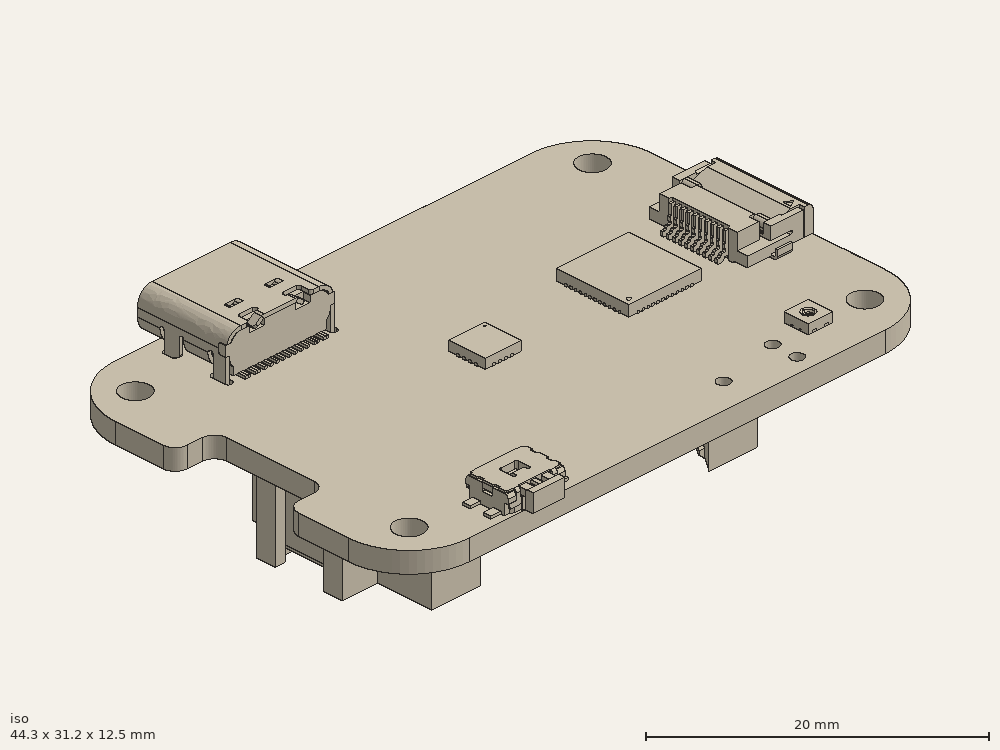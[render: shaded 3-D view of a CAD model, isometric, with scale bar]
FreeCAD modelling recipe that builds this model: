
FCSTD DOCUMENT  (FreeCAD 0.20R29410 (Git))
Label: case
License: All rights reserved
LicenseURL: http://en.wikipedia.org/wiki/All_rights_reserved
objects: Part::Feature×1, PartDesign::ShapeBinder×1, Sketcher::SketchObject×1, PartDesign::Body×1
note: 4 computed .brp shape members not serialized (recipe doc carries the construction recipe); baked Part::Feature solids carry a one-line shape summary decoded from their .brp

FEATURE [Part::Feature] Feature  label="PlantBuddy"
  Placement = pos=(-121,126,0) rot=(0,0,1;0rad)
  shape: bbox 44.33 x 31.16 x 12.48 mm, 3116 faces, 155 solids (baked)
FEATURE [PartDesign::ShapeBinder] ShapeBinder
  Placement = pos=(-143,126,0) rot=(0,0,1;0rad)
  Support = -> [Feature]
  TraceSupport = false
FEATURE [Sketcher::SketchObject] Sketch
  FullyConstrained = false
  MapMode = 5
  Support = -> [XY_Plane]
  sketch-geometry (4):
    g0: LineSegment StartX=-26.1099 StartY=15.4163 StartZ=0 EndX=26.1099 EndY=15.4163 EndZ=0
    g1: LineSegment StartX=26.1099 StartY=15.4163 StartZ=0 EndX=26.1099 EndY=-15.4163 EndZ=0
    g2: LineSegment StartX=26.1099 StartY=-15.4163 StartZ=0 EndX=-26.1099 EndY=-15.4163 EndZ=0
    g3: LineSegment StartX=-26.1099 StartY=-15.4163 StartZ=0 EndX=-26.1099 EndY=15.4163 EndZ=0
  constraints (9):
    c: Coincident(g0,g1)
    c: Coincident(g1,g2)
    c: Coincident(g2,g3)
    c: Coincident(g3,g0)
    c: Horizontal(g0)
    c: Horizontal(g2)
    c: Vertical(g1)
    c: Vertical(g3)
    c: Symmetric(g1,g0,g-1)
FEATURE [PartDesign::Body] Body
  Group = -> [ShapeBinder,Sketch]
  Origin = -> Origin
